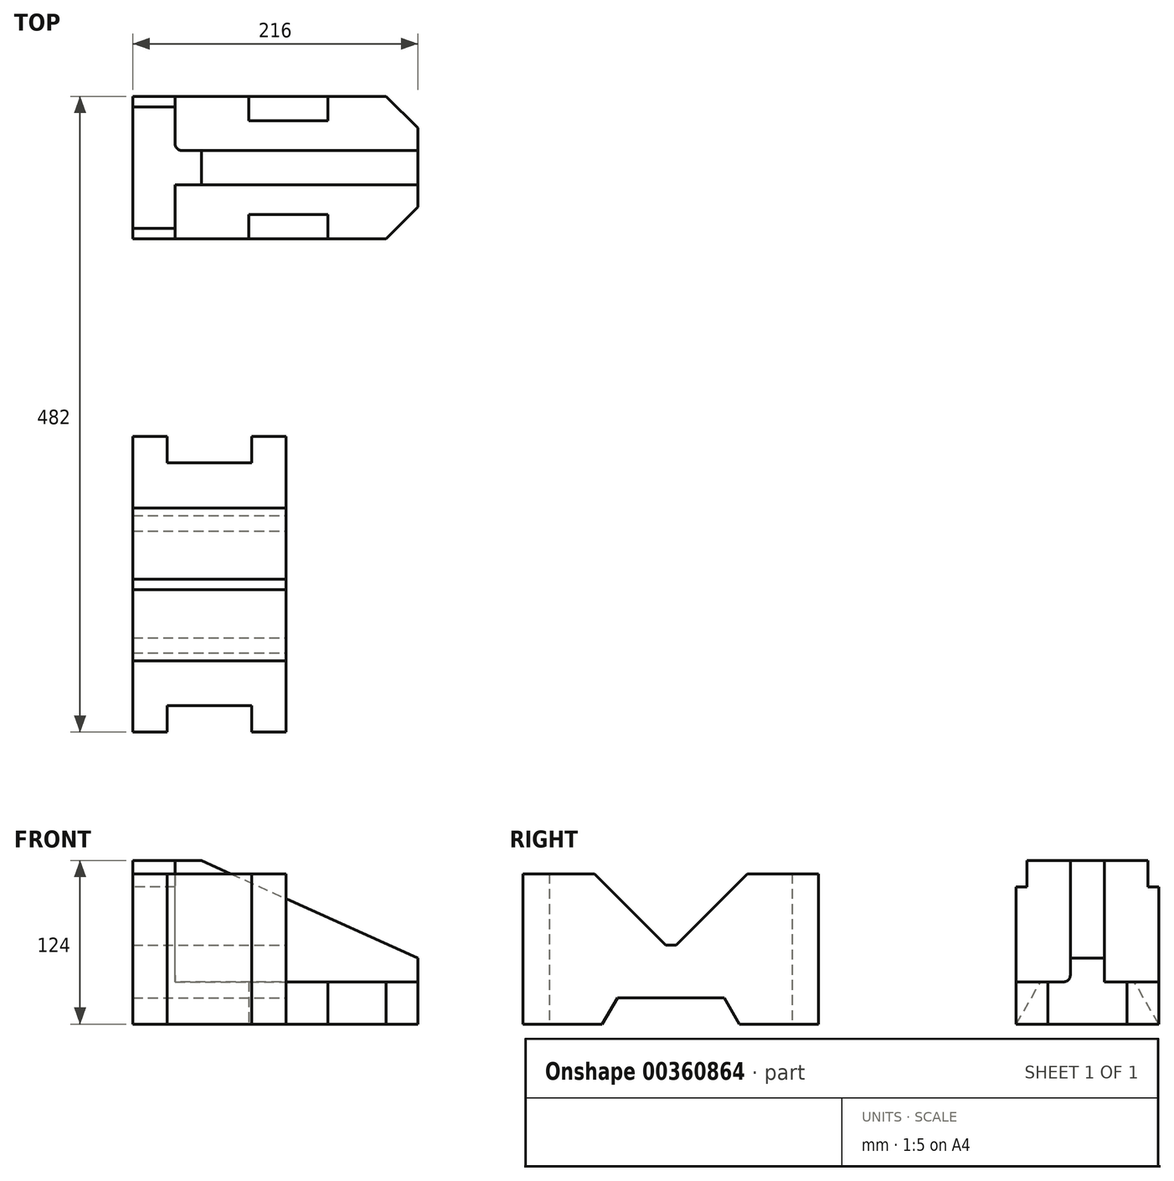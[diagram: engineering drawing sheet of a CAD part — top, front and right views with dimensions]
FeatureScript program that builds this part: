
annotation { "Feature Type Name" : "Feature", "Feature Type Description" : "" }
export const myFeature = defineFeature(function(context is Context, id is Id, definition is map)
    precondition{}
    {
        {
            var Q0;
            Q0=qCreatedBy(makeId("Top.planeOp"),FACE);
            var sketch = newSketch(context, id + "F0", { "sketchPlane" : qUnion([Q0])});
            skLineSegment(sketch, "E0", {"start": v(0, 0) * mm, "end": v(-58, 0) * mm});
            skLineSegment(sketch, "E1", {"start": v(-58, 0) * mm, "end": v(-58, 54) * mm});
            skLineSegment(sketch, "E2", {"start": v(-58, 54) * mm, "end": v(-58, 170) * mm});
            skLineSegment(sketch, "E3", {"start": v(-58, 170) * mm, "end": v(-58, 224) * mm});
            skPoint(sketch, "E3.endSnap0", {"position": v(-58, 112) * mm});
            skLineSegment(sketch, "E4", {"start": v(-58, 224) * mm, "end": v(-32, 224) * mm});
            skLineSegment(sketch, "E5", {"start": v(0, 224) * mm, "end": v(0, 0) * mm, "construction": true});
            skLineSegment(sketch, "E6.MirrorCS", {"start": v(58, 224) * mm, "end": v(32, 224) * mm});
            skLineSegment(sketch, "E7.MirrorCS", {"start": v(58, 170) * mm, "end": v(58, 224) * mm});
            skLineSegment(sketch, "E8.MirrorCS", {"start": v(58, 54) * mm, "end": v(58, 170) * mm});
            skLineSegment(sketch, "E9.MirrorCS", {"start": v(58, 0) * mm, "end": v(58, 54) * mm});
            skLineSegment(sketch, "E10.MirrorCS", {"start": v(32, 0) * mm, "end": v(58, 0) * mm});
            skLineSegment(sketch, "E11", {"start": v(-32, 0) * mm, "end": v(-32, 20) * mm});
            skLineSegment(sketch, "E12", {"start": v(-32, 20) * mm, "end": v(0, 20) * mm});
            skLineSegment(sketch, "E13", {"start": v(-58, 112) * mm, "end": v(58, 112) * mm, "construction": true});
            skLineSegment(sketch, "E14.MirrorCS", {"start": v(32, 20) * mm, "end": v(0, 20) * mm});
            skLineSegment(sketch, "E15.MirrorCS", {"start": v(32, 0) * mm, "end": v(32, 20) * mm});
            skLineSegment(sketch, "E16.MirrorCS", {"start": v(-32, 204) * mm, "end": v(0, 204) * mm});
            skLineSegment(sketch, "E17.MirrorCS", {"start": v(32, 204) * mm, "end": v(0, 204) * mm});
            skLineSegment(sketch, "E18.MirrorCS", {"start": v(-32, 224) * mm, "end": v(-32, 204) * mm});
            skLineSegment(sketch, "E19.MirrorCS", {"start": v(32, 224) * mm, "end": v(32, 204) * mm});
            skPoint(sketch, "E20.orphan", {"position": v(0, 0) * mm});
            skPoint(sketch, "E21.orphan", {"position": v(0, 224) * mm});
            skSolve(sketch);
        }
        {
            var Q0;
            Q0 = qSketchRegion(id + "F0", true);
            extrude(context, id + "F1", {"entities" : qUnion([Q0]), "depth" : 114 * mm});
        }
        {
            var Q0;
            Q0=makeQuery(id+"F1.opExtrude","SWEPT_FACE",FACE,{"disambiguationData":[OSD([sQuery(id+"F0.wireOp",EDGE,"E7.MirrorCS"),sQuery(id+"F0.wireOp",EDGE,"E8.MirrorCS"),sQuery(id+"F0.wireOp",EDGE,"E9.MirrorCS")])]});
            var sketch = newSketch(context, id + "F2", { "sketchPlane" : qUnion([Q0])});
            skPoint(sketch, "E22.0", {"position": v(54, 0) * mm});
            skPoint(sketch, "E23.0", {"position": v(170, 0) * mm});
            skLineSegment(sketch, "E24", {"start": v(54, 0) * mm, "end": v(54, 114) * mm, "construction": true});
            skLineSegment(sketch, "E25", {"start": v(170, 0) * mm, "end": v(170, 114) * mm, "construction": true});
            skLineSegment(sketch, "E26", {"start": v(0, 0) * mm, "end": v(60, 0) * mm, "construction": true});
            skLineSegment(sketch, "E27", {"start": v(224, 0) * mm, "end": v(164, 0) * mm, "construction": true});
            skLineSegment(sketch, "E28", {"start": v(60, 0) * mm, "end": v(164, 0) * mm});
            skLineSegment(sketch, "E29", {"start": v(54, 0) * mm, "end": v(54, 20) * mm, "construction": true});
            skLineSegment(sketch, "E30", {"start": v(71.55, 20) * mm, "end": v(152.45, 20) * mm, "construction": true});
            skLineSegment(sketch, "E31", {"start": v(60, 0) * mm, "end": v(71.55, 20) * mm});
            skLineSegment(sketch, "E32", {"start": v(164, 0) * mm, "end": v(152.45, 20) * mm});
            skLineSegment(sketch, "E33", {"start": v(71.55, 20) * mm, "end": v(152.45, 20) * mm});
            skLineSegment(sketch, "E34", {"start": v(54, 114) * mm, "end": v(170, 114) * mm});
            skLineSegment(sketch, "E35", {"start": v(71.55, 20) * mm, "end": v(71.55, 60) * mm, "construction": true});
            skLineSegment(sketch, "E36", {"start": v(71.55, 60) * mm, "end": v(152.45, 60) * mm, "construction": true});
            skLineSegment(sketch, "E37", {"start": v(54, 114) * mm, "end": v(108, 60) * mm});
            skLineSegment(sketch, "E38", {"start": v(170, 114) * mm, "end": v(116, 60) * mm});
            skLineSegment(sketch, "E39", {"start": v(108, 60) * mm, "end": v(116, 60) * mm});
            skSolve(sketch);
        }
        {
            var Q0;
            Q0 = qSketchRegion(id + "F2", true);
            extrude(context, id + "F3", {"entities" : qUnion([Q0]), "operationType" : NewBodyOperationType.REMOVE, "endBound" : BoundingType.THROUGH_ALL, "oppositeDirection" : true, "depth" : 25 * mm});
        }
        {
            var Q0;
            Q0=qCreatedBy(makeId("Top.planeOp"),FACE);
            var sketch = newSketch(context, id + "F4", { "sketchPlane" : qUnion([Q0])});
            skPoint(sketch, "E40.0", {"position": v(-58, 224) * mm});
            skLineSegment(sketch, "E41", {"start": v(-58, 224) * mm, "end": v(-58, 374) * mm, "construction": true});
            skLineSegment(sketch, "E42", {"start": v(-58, 374) * mm, "end": v(30, 374) * mm});
            skLineSegment(sketch, "E43", {"start": v(30, 374) * mm, "end": v(90, 374) * mm});
            skLineSegment(sketch, "E44", {"start": v(90, 374) * mm, "end": v(158, 374) * mm});
            skLineSegment(sketch, "E45", {"start": v(158, 374) * mm, "end": v(158, 482) * mm});
            skLineSegment(sketch, "E46", {"start": v(158, 482) * mm, "end": v(90, 482) * mm});
            skLineSegment(sketch, "E47", {"start": v(90, 482) * mm, "end": v(30, 482) * mm});
            skLineSegment(sketch, "E48", {"start": v(30, 482) * mm, "end": v(-58, 482) * mm});
            skLineSegment(sketch, "E49", {"start": v(-58, 482) * mm, "end": v(-58, 374) * mm});
            skSolve(sketch);
        }
        {
            var Q0;
            Q0 = qSketchRegion(id + "F4", true);
            extrude(context, id + "F5", {"entities" : qUnion([Q0]), "depth" : 32 * mm});
        }
        {
            var Q0;
            Q0=makeQuery(id+"F5.opExtrude","SWEPT_EDGE",EDGE,{"disambiguationData":[OSD([sQuery(id+"F4.wireOp",EDGE,"E44"),sQuery(id+"F4.wireOp",EDGE,"E45")])]});
            var Q1;
            Q1=makeQuery(id+"F5.opExtrude","SWEPT_EDGE",EDGE,{"disambiguationData":[OSD([sQuery(id+"F4.wireOp",EDGE,"E45"),sQuery(id+"F4.wireOp",EDGE,"E46")])]});
            chamfer(context, id + "F6", {"entities" : qUnion([Q0, Q1]), "width" : 24 * mm, "tangentPropagation" : true});
        }
        {
            var Q0;
            Q0=makeQuery(id+"F5.opExtrude","SWEPT_FACE",FACE,{"disambiguationData":[OSD([sQuery(id+"F4.wireOp",EDGE,"E45")])]});
            cPlane(context, id + "F7", {"entities" : qUnion([Q0]), "cplaneType" : CPlaneType.OFFSET, "offset" : 68 * mm, "oppositeDirection" : true, "width" : 150 * mm, "height" : 150 * mm});
        }
        {
            var Q0;
            Q0=qCreatedBy(id+"F7.planeOp",FACE);
            var sketch = newSketch(context, id + "F8", { "sketchPlane" : qUnion([Q0])});
            skPoint(sketch, "E50.0", {"position": v(374, 0) * mm});
            skPoint(sketch, "E51.0", {"position": v(482, 0) * mm});
            skLineSegment(sketch, "E52.0", {"start": v(374, 32) * mm, "end": v(374, 0) * mm});
            skLineSegment(sketch, "E53.0", {"start": v(482, 32) * mm, "end": v(482, 0) * mm});
            skLineSegment(sketch, "E54", {"start": v(374, 0) * mm, "end": v(482, 0) * mm, "construction": true});
            skLineSegment(sketch, "E55", {"start": v(374, 32) * mm, "end": v(482, 32) * mm, "construction": true});
            skLineSegment(sketch, "E56", {"start": v(374, 0) * mm, "end": v(392.48, 32) * mm});
            skLineSegment(sketch, "E57", {"start": v(482, 0) * mm, "end": v(463.52, 32) * mm});
            skLineSegment(sketch, "E58", {"start": v(374, 32) * mm, "end": v(392.48, 32) * mm});
            skLineSegment(sketch, "E59", {"start": v(463.52, 32) * mm, "end": v(482, 32) * mm});
            skSolve(sketch);
        }
        {
            var Q0;
            Q0 = qSketchRegion(id + "F8", true);
            extrude(context, id + "F9", {"entities" : qUnion([Q0]), "operationType" : NewBodyOperationType.REMOVE, "oppositeDirection" : true, "depth" : 60 * mm});
        }
        {
            var Q0;
            Q0=makeQuery(id+"F5.opExtrude","SWEPT_FACE",FACE,{"disambiguationData":[OSD([sQuery(id+"F4.wireOp",EDGE,"E49")])]});
            var sketch = newSketch(context, id + "F10", { "sketchPlane" : qUnion([Q0])});
            skLineSegment(sketch, "E60", {"start": v(-482, 32) * mm, "end": v(-482, 104) * mm});
            skLineSegment(sketch, "E61", {"start": v(-474, 124) * mm, "end": v(-382, 124) * mm});
            skLineSegment(sketch, "E62", {"start": v(-374, 104) * mm, "end": v(-374, 32) * mm});
            skLineSegment(sketch, "E63.top", {"start": v(-482, 104) * mm, "end": v(-474, 104) * mm});
            skLineSegment(sketch, "E63.right", {"start": v(-474, 124) * mm, "end": v(-474, 104) * mm});
            skLineSegment(sketch, "E64.top", {"start": v(-374, 104) * mm, "end": v(-382, 104) * mm});
            skLineSegment(sketch, "E64.right", {"start": v(-382, 124) * mm, "end": v(-382, 104) * mm});
            skPoint(sketch, "E64.bottom.start.orphan", {"position": v(-374, 124) * mm});
            skLineSegment(sketch, "E65", {"start": v(-482, 32) * mm, "end": v(-374, 32) * mm});
            skSolve(sketch);
        }
        {
            var Q0;
            Q0 = qSketchRegion(id + "F10", true);
            extrude(context, id + "F11", {"entities" : qUnion([Q0]), "operationType" : NewBodyOperationType.ADD, "oppositeDirection" : true, "depth" : 32 * mm});
        }
        {
            var Q0;
            {var subQ1=sQuery(id+"F4.wireOp",EDGE,"E49");var subQ2=sQuery(id+"F4.wireOp",EDGE,"E48");var subQ3=sQuery(id+"F4.wireOp",EDGE,"E47");var subQ4=sQuery(id+"F4.wireOp",EDGE,"E46");Q0=makeQuery(id+"F11.boolean.opBoolean","MERGE",FACE,{"derivedFrom":[makeQuery(id+"F9.boolean.opBoolean","SPLIT",FACE,{"disambiguationData":[TD([makeQuery(id+"F5.opExtrude","SWEPT_FACE",FACE,{"disambiguationData":[OSD([subQ1])]})])],"derivedFrom":makeQuery(id+"F5.opExtrude","SWEPT_FACE",FACE,{"disambiguationData":[OSD([subQ4,subQ3,subQ2])]})}),makeQuery(id+"F11.opExtrude","SWEPT_FACE",FACE,{"disambiguationData":[OSD([sQuery(id+"F10.wireOp",EDGE,"E60")])]})]});}
            cPlane(context, id + "F12", {"entities" : qUnion([Q0]), "cplaneType" : CPlaneType.OFFSET, "offset" : 54 * mm, "oppositeDirection" : true, "width" : 150 * mm, "height" : 150 * mm});
        }
        {
            var Q0;
            Q0=qCreatedBy(id+"F12.planeOp",FACE);
            var sketch = newSketch(context, id + "F13", { "sketchPlane" : qUnion([Q0])});
            skLineSegment(sketch, "E66.0", {"start": v(26, 32) * mm, "end": v(26, 104) * mm});
            skLineSegment(sketch, "E67.0", {"start": v(26, 124) * mm, "end": v(26, 104) * mm});
            skLineSegment(sketch, "E68.0", {"start": v(-158, 32) * mm, "end": v(-134, 32) * mm});
            skLineSegment(sketch, "E69", {"start": v(-134, 32) * mm, "end": v(26, 32) * mm});
            skLineSegment(sketch, "E70", {"start": v(-158, 32) * mm, "end": v(-158, 50) * mm});
            skLineSegment(sketch, "E71", {"start": v(26, 124) * mm, "end": v(6, 124) * mm});
            skLineSegment(sketch, "E72", {"start": v(6, 124) * mm, "end": v(-158, 50) * mm});
            skSolve(sketch);
        }
        {
            var Q0;
            Q0 = qSketchRegion(id + "F13", true);
            extrude(context, id + "F14", {"entities" : qUnion([Q0]), "operationType" : NewBodyOperationType.ADD, "endBound" : BoundingType.SYMMETRIC, "depth" : 26 * mm});
        }
        {
            var Q0;
            Q0=makeQuery(id+"F14.opExtrude","CAP_EDGE",EDGE,{"disambiguationData":[OSD([sQuery(id+"F13.wireOp",EDGE,"E66.0"),sQuery(id+"F13.wireOp",EDGE,"E67.0")])],"isStart":true});
            var Q1;
            Q1=makeQuery(id+"F14.opExtrude","CAP_EDGE",EDGE,{"disambiguationData":[OSD([sQuery(id+"F13.wireOp",EDGE,"E68.0"),sQuery(id+"F13.wireOp",EDGE,"E69")])],"isStart":true});
            var Q2;
            {var subQ0=sQuery(id+"F10.wireOp",EDGE,"E62");var subQ1=sQuery(id+"F10.wireOp",EDGE,"E65");Q2=makeQuery(id+"F14.boolean.opBoolean","SPLIT",EDGE,{"disambiguationData":[TD([makeQuery(id+"F11.opExtrude","SWEPT_FACE",FACE,{"disambiguationData":[OSD([subQ0])]})])],"derivedFrom":makeQuery(id+"F11.opExtrude","CAP_EDGE",EDGE,{"disambiguationData":[OSD([subQ1])],"isStart":false})});}
            var Q3;
            Q3=makeQuery(id+"F14.opExtrude","CAP_EDGE",EDGE,{"disambiguationData":[OSD([sQuery(id+"F13.wireOp",EDGE,"E68.0"),sQuery(id+"F13.wireOp",EDGE,"E69")])],"isStart":false});
            var Q4;
            {var subQ0=sQuery(id+"F10.wireOp",EDGE,"E65");var subQ1=sQuery(id+"F10.wireOp",EDGE,"E60");Q4=makeQuery(id+"F14.boolean.opBoolean","SPLIT",EDGE,{"disambiguationData":[TD([makeQuery(id+"F11.opExtrude","SWEPT_FACE",FACE,{"disambiguationData":[OSD([subQ1])]})])],"derivedFrom":makeQuery(id+"F11.opExtrude","CAP_EDGE",EDGE,{"disambiguationData":[OSD([subQ0])],"isStart":false})});}
            var Q5;
            Q5=makeQuery(id+"F14.opExtrude","CAP_EDGE",EDGE,{"disambiguationData":[OSD([sQuery(id+"F13.wireOp",EDGE,"E66.0"),sQuery(id+"F13.wireOp",EDGE,"E67.0")])],"isStart":false});
            fillet(context, id + "F15", {"entities" : qUnion([Q0, Q1, Q2, Q3, Q4, Q5]), "radius" : 5 * mm, "tangentPropagation" : true, "allowEdgeOverflow" : false});
        }
    });
